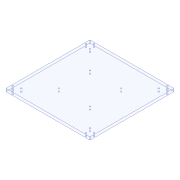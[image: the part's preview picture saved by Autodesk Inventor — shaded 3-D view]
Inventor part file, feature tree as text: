
AUTODESK INVENTOR PART (.ipt)
format: ipt  version: 2020 (Build 240168000, 168)  size: 137,216 bytes
history: native  units: mm
features: extrude x2, sketch x2, other x1
ambient origin geometry x8: Origin, YZ Plane, XZ Plane, XY Plane, X Axis, Y Axis, Z Axis, Center Point
bodies: Solid1 (feature_tree)
feature tree (5):
  extrude  "Extrusion1"  Depth=148.5mm
  extrude  "Extrusion2"  Depth=10.0mm
  sketch  "Sketch2"  dims[d2=148.5mm d3=148.5mm]
  sketch  "Sketch3"  dims[d4=110.0mm d5=110.0mm d6=4.0mm d7=4.0mm d8=4.0mm d9=4.0mm d10=10.0mm d11=0.0mm d12=10.0mm d13=0.0mm]
  other  "Cut-Extrude14"
